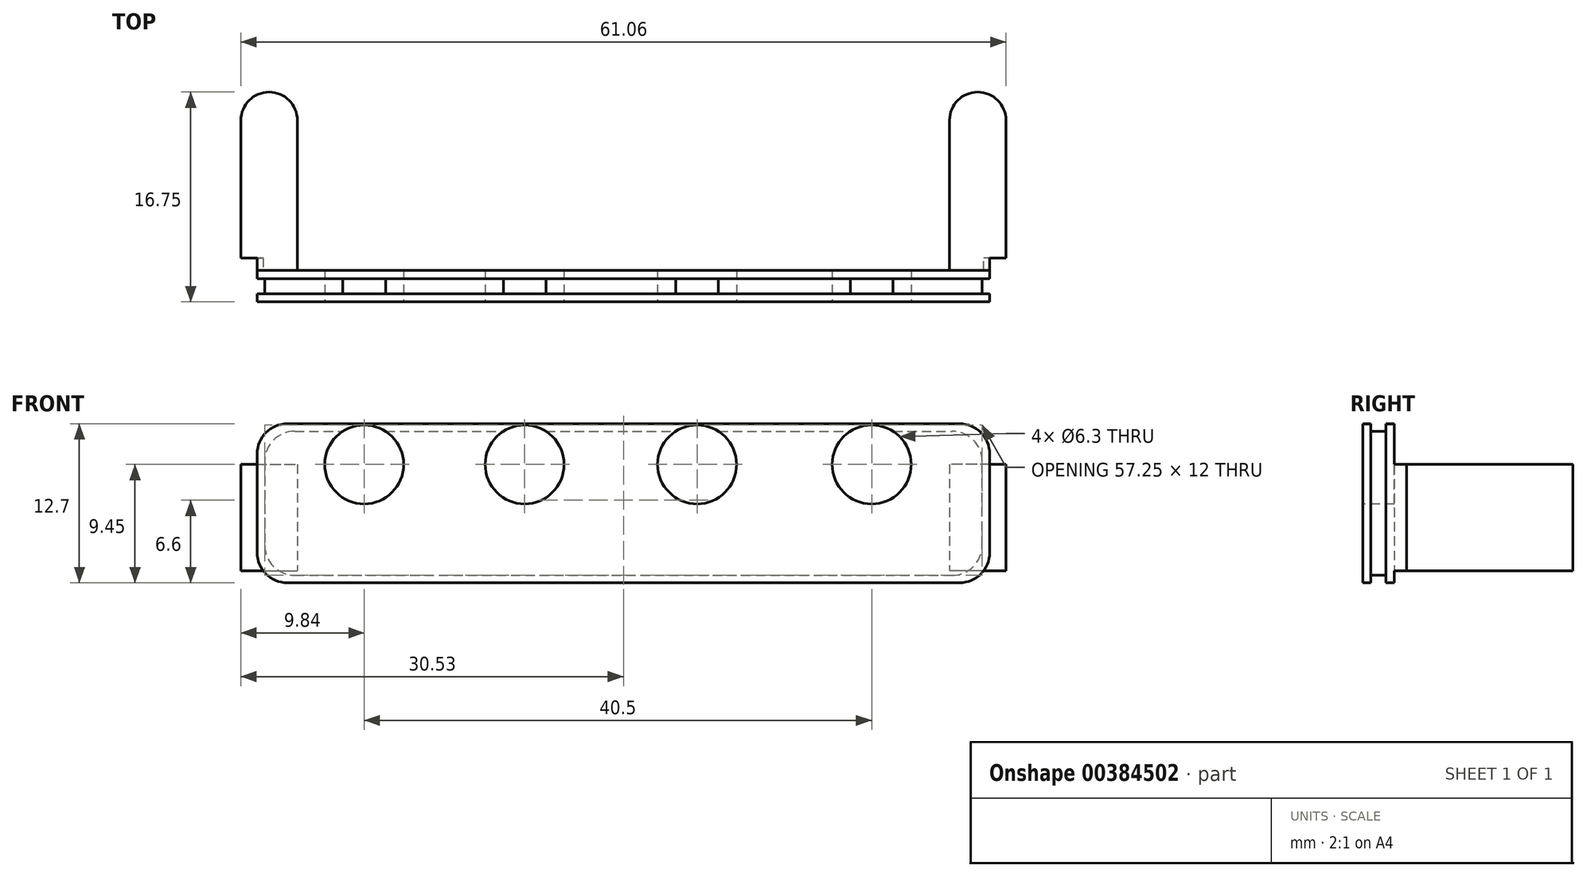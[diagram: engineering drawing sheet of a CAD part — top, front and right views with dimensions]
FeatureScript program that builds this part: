
annotation { "Feature Type Name" : "Feature", "Feature Type Description" : "" }
export const myFeature = defineFeature(function(context is Context, id is Id, definition is map)
    precondition{}
    {
        {
            var Q0;
            Q0=qCreatedBy(makeId("Front.planeOp"),FACE);
            var sketch = newSketch(context, id + "F0", { "sketchPlane" : qUnion([Q0])});
            skLineSegment(sketch, "E0.bottom", {"start": v(29.22, -6.35) * mm, "end": v(-29.23, -6.35) * mm});
            skLineSegment(sketch, "E0.top", {"start": v(29.23, 6.35) * mm, "end": v(-29.23, 6.35) * mm});
            skLineSegment(sketch, "E0.left", {"start": v(29.23, -6.35) * mm, "end": v(29.23, 6.35) * mm});
            skLineSegment(sketch, "E0.right", {"start": v(-29.23, -6.35) * mm, "end": v(-29.23, 6.35) * mm});
            skPoint(sketch, "E0.middle", {"position": v(0, 0) * mm});
            skSolve(sketch);
        }
        {
            var Q0;
            Q0 = qSketchRegion(id + "F0", true);
            extrude(context, id + "F1", {"entities" : qUnion([Q0]), "oppositeDirection" : true, "depth" : 2.5 * mm});
        }
        {
            var Q0;
            Q0=makeQuery(id+"F1.opExtrude","SWEPT_FACE",FACE,{"disambiguationData":[OSD([sQuery(id+"F0.wireOp",EDGE,"E0.top")])]});
            var sketch = newSketch(context, id + "F2", { "sketchPlane" : qUnion([Q0])});
            skLineSegment(sketch, "E1.bottom", {"start": v(-29.23, 1.85) * mm, "end": v(29.23, 1.85) * mm});
            skLineSegment(sketch, "E1.top", {"start": v(-29.23, 0.64) * mm, "end": v(29.23, 0.64) * mm});
            skLineSegment(sketch, "E1.left", {"start": v(-29.23, 1.85) * mm, "end": v(-29.23, 0.64) * mm});
            skLineSegment(sketch, "E1.right", {"start": v(29.23, 1.85) * mm, "end": v(29.23, 0.64) * mm});
            skSolve(sketch);
        }
        {
            var Q0;
            Q0=makeQuery(id+"F1.opExtrude","SWEPT_FACE",FACE,{"disambiguationData":[OSD([sQuery(id+"F0.wireOp",EDGE,"E0.right")])]});
            var sketch = newSketch(context, id + "F3", { "sketchPlane" : qUnion([Q0])});
            skLineSegment(sketch, "E2.bottom", {"start": v(-1.85, 6.35) * mm, "end": v(-0.64, 6.35) * mm});
            skLineSegment(sketch, "E2.top", {"start": v(-1.85, -6.35) * mm, "end": v(-0.64, -6.35) * mm});
            skLineSegment(sketch, "E2.left", {"start": v(-1.85, 6.35) * mm, "end": v(-1.85, -6.35) * mm});
            skLineSegment(sketch, "E2.right", {"start": v(-0.64, 6.35) * mm, "end": v(-0.64, -6.35) * mm});
            skSolve(sketch);
        }
        {
            var Q0;
            Q0=makeQuery(id+"F1.opExtrude","SWEPT_FACE",FACE,{"disambiguationData":[OSD([sQuery(id+"F0.wireOp",EDGE,"E0.bottom")])]});
            var sketch = newSketch(context, id + "F4", { "sketchPlane" : qUnion([Q0])});
            skLineSegment(sketch, "E3.bottom", {"start": v(-29.23, -1.85) * mm, "end": v(29.23, -1.85) * mm});
            skLineSegment(sketch, "E3.top", {"start": v(-29.23, -0.64) * mm, "end": v(29.23, -0.64) * mm});
            skLineSegment(sketch, "E3.left", {"start": v(-29.23, -1.85) * mm, "end": v(-29.23, -0.64) * mm});
            skLineSegment(sketch, "E3.right", {"start": v(29.22, -1.85) * mm, "end": v(29.22, -0.64) * mm});
            skSolve(sketch);
        }
        {
            var Q0;
            Q0=makeQuery(id+"F1.opExtrude","SWEPT_FACE",FACE,{"disambiguationData":[OSD([sQuery(id+"F0.wireOp",EDGE,"E0.left")])]});
            var sketch = newSketch(context, id + "F5", { "sketchPlane" : qUnion([Q0])});
            skLineSegment(sketch, "E4.bottom", {"start": v(1.85, -6.35) * mm, "end": v(0.64, -6.35) * mm});
            skLineSegment(sketch, "E4.top", {"start": v(1.85, 6.35) * mm, "end": v(0.64, 6.35) * mm});
            skLineSegment(sketch, "E4.left", {"start": v(1.85, -6.35) * mm, "end": v(1.85, 6.35) * mm});
            skLineSegment(sketch, "E4.right", {"start": v(0.64, -6.35) * mm, "end": v(0.64, 6.35) * mm});
            skSolve(sketch);
        }
        {
            var Q0;
            Q0=makeQuery(id+"F2.imprint","IMPRINT",FACE,{"disambiguationData":[TD([[makeQuery(id+"F2.imprint","IMPRINT",EDGE,{"derivedFrom":sQuery(id+"F2.wireOp",EDGE,"E1.bottom")}),-1.0]])]});
            extrude(context, id + "F6", {"entities" : qUnion([Q0]), "operationType" : NewBodyOperationType.REMOVE, "oppositeDirection" : true, "depth" : 0.6 * mm});
        }
        {
            var Q0;
            Q0=makeQuery(id+"F4.imprint","IMPRINT",FACE,{"disambiguationData":[TD([[makeQuery(id+"F4.imprint","IMPRINT",EDGE,{"derivedFrom":sQuery(id+"F4.wireOp",EDGE,"E3.bottom")}),1.0]])]});
            extrude(context, id + "F7", {"entities" : qUnion([Q0]), "operationType" : NewBodyOperationType.REMOVE, "oppositeDirection" : true, "depth" : 0.6 * mm});
        }
        {
            var Q0;
            Q0=makeQuery(id+"F5.imprint","IMPRINT",FACE,{"disambiguationData":[TD([[makeQuery(id+"F5.imprint","IMPRINT",EDGE,{"derivedFrom":sQuery(id+"F5.wireOp",EDGE,"E4.bottom")}),-1.0]])]});
            extrude(context, id + "F8", {"entities" : qUnion([Q0]), "operationType" : NewBodyOperationType.REMOVE, "oppositeDirection" : true, "depth" : 0.6 * mm});
        }
        {
            var Q0;
            Q0=makeQuery(id+"F3.imprint","IMPRINT",FACE,{"disambiguationData":[TD([[makeQuery(id+"F3.imprint","IMPRINT",EDGE,{"derivedFrom":sQuery(id+"F3.wireOp",EDGE,"E2.bottom")}),-1.0]])]});
            extrude(context, id + "F9", {"entities" : qUnion([Q0]), "operationType" : NewBodyOperationType.REMOVE, "oppositeDirection" : true, "depth" : 0.6 * mm});
        }
        {
            var Q0;
            Q0=makeQuery(id+"F1.opExtrude","CAP_FACE",FACE,{"disambiguationData":[OSD([sQuery(id+"F0.wireOp",EDGE,"E0.bottom"),sQuery(id+"F0.wireOp",EDGE,"E0.top"),sQuery(id+"F0.wireOp",EDGE,"E0.left"),sQuery(id+"F0.wireOp",EDGE,"E0.right")])],"isStart":false});
            var sketch = newSketch(context, id + "F10", { "sketchPlane" : qUnion([Q0])});
            skLineSegment(sketch, "E5.bottom", {"start": v(-29.23, 3.1) * mm, "end": v(-26.02, 3.1) * mm});
            skLineSegment(sketch, "E5.top", {"start": v(-29.23, -5.4) * mm, "end": v(-26.02, -5.4) * mm});
            skLineSegment(sketch, "E5.left", {"start": v(-29.23, 3.1) * mm, "end": v(-29.23, -5.4) * mm});
            skLineSegment(sketch, "E5.right", {"start": v(-26.02, 3.1) * mm, "end": v(-26.02, -5.4) * mm});
            skLineSegment(sketch, "E6.bottom", {"start": v(29.23, 3.1) * mm, "end": v(26.02, 3.1) * mm});
            skLineSegment(sketch, "E6.top", {"start": v(29.23, -5.4) * mm, "end": v(26.02, -5.4) * mm});
            skLineSegment(sketch, "E6.left", {"start": v(29.23, 3.1) * mm, "end": v(29.23, -5.4) * mm});
            skLineSegment(sketch, "E6.right", {"start": v(26.02, 3.1) * mm, "end": v(26.02, -5.4) * mm});
            skSolve(sketch);
        }
        {
            var Q0;
            Q0 = qSketchRegion(id + "F10", true);
            extrude(context, id + "F11", {"entities" : qUnion([Q0]), "operationType" : NewBodyOperationType.ADD, "depth" : 1 * mm});
        }
        {
            var Q0;
            {var subQ0=sQuery(id+"F0.wireOp",EDGE,"E0.bottom");var subQ1=sQuery(id+"F0.wireOp",EDGE,"E0.right");Q0=makeQuery(id+"F7.boolean.opBoolean","SPLIT",EDGE,{"disambiguationData":[TD([makeQuery(id+"F7.opExtrude","SWEPT_FACE",FACE,{"disambiguationData":[OSD([sQuery(id+"F4.wireOp",EDGE,"E3.bottom")])]})])],"derivedFrom":makeQuery(id+"F1.opExtrude","SWEPT_EDGE",EDGE,{"disambiguationData":[OSD([subQ0,subQ1])]})});}
            var Q1;
            Q1=makeQuery(id+"F9.boolean.opBoolean","INTERSECT",EDGE,{"derivedFrom":[makeQuery(id+"F7.boolean.opBoolean","COPY",FACE,{"derivedFrom":makeQuery(id+"F7.opExtrude","CAP_FACE",FACE,{"disambiguationData":[OSD([sQuery(id+"F4.wireOp",EDGE,"E3.bottom"),sQuery(id+"F4.wireOp",EDGE,"E3.top"),sQuery(id+"F4.wireOp",EDGE,"E3.left"),sQuery(id+"F4.wireOp",EDGE,"E3.right")])],"isStart":false})}),makeQuery(id+"F9.opExtrude","CAP_FACE",FACE,{"disambiguationData":[OSD([sQuery(id+"F3.wireOp",EDGE,"E2.bottom"),sQuery(id+"F3.wireOp",EDGE,"E2.top"),sQuery(id+"F3.wireOp",EDGE,"E2.left"),sQuery(id+"F3.wireOp",EDGE,"E2.right")])],"isStart":false})]});
            var Q2;
            {var subQ0=sQuery(id+"F0.wireOp",EDGE,"E0.bottom");var subQ1=sQuery(id+"F0.wireOp",EDGE,"E0.right");Q2=makeQuery(id+"F7.boolean.opBoolean","SPLIT",EDGE,{"disambiguationData":[TD([makeQuery(id+"F7.opExtrude","SWEPT_FACE",FACE,{"disambiguationData":[OSD([sQuery(id+"F4.wireOp",EDGE,"E3.top")])]})])],"derivedFrom":makeQuery(id+"F1.opExtrude","SWEPT_EDGE",EDGE,{"disambiguationData":[OSD([subQ0,subQ1])]})});}
            var Q3;
            {var subQ0=sQuery(id+"F0.wireOp",EDGE,"E0.right");var subQ1=sQuery(id+"F0.wireOp",EDGE,"E0.top");Q3=makeQuery(id+"F6.boolean.opBoolean","SPLIT",EDGE,{"disambiguationData":[TD([makeQuery(id+"F6.opExtrude","SWEPT_FACE",FACE,{"disambiguationData":[OSD([sQuery(id+"F2.wireOp",EDGE,"E1.top")])]})])],"derivedFrom":makeQuery(id+"F1.opExtrude","SWEPT_EDGE",EDGE,{"disambiguationData":[OSD([subQ1,subQ0])]})});}
            var Q4;
            Q4=makeQuery(id+"F9.boolean.opBoolean","INTERSECT",EDGE,{"derivedFrom":[makeQuery(id+"F6.boolean.opBoolean","COPY",FACE,{"derivedFrom":makeQuery(id+"F6.opExtrude","CAP_FACE",FACE,{"disambiguationData":[OSD([sQuery(id+"F2.wireOp",EDGE,"E1.bottom"),sQuery(id+"F2.wireOp",EDGE,"E1.top"),sQuery(id+"F2.wireOp",EDGE,"E1.left"),sQuery(id+"F2.wireOp",EDGE,"E1.right")])],"isStart":false})}),makeQuery(id+"F9.opExtrude","CAP_FACE",FACE,{"disambiguationData":[OSD([sQuery(id+"F3.wireOp",EDGE,"E2.bottom"),sQuery(id+"F3.wireOp",EDGE,"E2.top"),sQuery(id+"F3.wireOp",EDGE,"E2.left"),sQuery(id+"F3.wireOp",EDGE,"E2.right")])],"isStart":false})]});
            var Q5;
            {var subQ0=sQuery(id+"F0.wireOp",EDGE,"E0.right");var subQ1=sQuery(id+"F0.wireOp",EDGE,"E0.top");Q5=makeQuery(id+"F6.boolean.opBoolean","SPLIT",EDGE,{"disambiguationData":[TD([makeQuery(id+"F6.opExtrude","SWEPT_FACE",FACE,{"disambiguationData":[OSD([sQuery(id+"F2.wireOp",EDGE,"E1.bottom")])]})])],"derivedFrom":makeQuery(id+"F1.opExtrude","SWEPT_EDGE",EDGE,{"disambiguationData":[OSD([subQ1,subQ0])]})});}
            var Q6;
            {var subQ0=sQuery(id+"F0.wireOp",EDGE,"E0.left");var subQ1=sQuery(id+"F0.wireOp",EDGE,"E0.top");Q6=makeQuery(id+"F6.boolean.opBoolean","SPLIT",EDGE,{"disambiguationData":[TD([makeQuery(id+"F6.opExtrude","SWEPT_FACE",FACE,{"disambiguationData":[OSD([sQuery(id+"F2.wireOp",EDGE,"E1.top")])]})])],"derivedFrom":makeQuery(id+"F1.opExtrude","SWEPT_EDGE",EDGE,{"disambiguationData":[OSD([subQ1,subQ0])]})});}
            var Q7;
            Q7=makeQuery(id+"F8.boolean.opBoolean","INTERSECT",EDGE,{"derivedFrom":[makeQuery(id+"F6.boolean.opBoolean","COPY",FACE,{"derivedFrom":makeQuery(id+"F6.opExtrude","CAP_FACE",FACE,{"disambiguationData":[OSD([sQuery(id+"F2.wireOp",EDGE,"E1.bottom"),sQuery(id+"F2.wireOp",EDGE,"E1.top"),sQuery(id+"F2.wireOp",EDGE,"E1.left"),sQuery(id+"F2.wireOp",EDGE,"E1.right")])],"isStart":false})}),makeQuery(id+"F8.opExtrude","CAP_FACE",FACE,{"disambiguationData":[OSD([sQuery(id+"F5.wireOp",EDGE,"E4.bottom"),sQuery(id+"F5.wireOp",EDGE,"E4.top"),sQuery(id+"F5.wireOp",EDGE,"E4.left"),sQuery(id+"F5.wireOp",EDGE,"E4.right")])],"isStart":false})]});
            var Q8;
            {var subQ0=sQuery(id+"F0.wireOp",EDGE,"E0.left");var subQ1=sQuery(id+"F0.wireOp",EDGE,"E0.top");Q8=makeQuery(id+"F6.boolean.opBoolean","SPLIT",EDGE,{"disambiguationData":[TD([makeQuery(id+"F6.opExtrude","SWEPT_FACE",FACE,{"disambiguationData":[OSD([sQuery(id+"F2.wireOp",EDGE,"E1.bottom")])]})])],"derivedFrom":makeQuery(id+"F1.opExtrude","SWEPT_EDGE",EDGE,{"disambiguationData":[OSD([subQ1,subQ0])]})});}
            var Q9;
            {var subQ0=sQuery(id+"F0.wireOp",EDGE,"E0.bottom");var subQ1=sQuery(id+"F0.wireOp",EDGE,"E0.left");Q9=makeQuery(id+"F7.boolean.opBoolean","SPLIT",EDGE,{"disambiguationData":[TD([makeQuery(id+"F7.opExtrude","SWEPT_FACE",FACE,{"disambiguationData":[OSD([sQuery(id+"F4.wireOp",EDGE,"E3.top")])]})])],"derivedFrom":makeQuery(id+"F1.opExtrude","SWEPT_EDGE",EDGE,{"disambiguationData":[OSD([subQ0,subQ1])]})});}
            var Q10;
            Q10=makeQuery(id+"F8.boolean.opBoolean","INTERSECT",EDGE,{"derivedFrom":[makeQuery(id+"F7.boolean.opBoolean","COPY",FACE,{"derivedFrom":makeQuery(id+"F7.opExtrude","CAP_FACE",FACE,{"disambiguationData":[OSD([sQuery(id+"F4.wireOp",EDGE,"E3.bottom"),sQuery(id+"F4.wireOp",EDGE,"E3.top"),sQuery(id+"F4.wireOp",EDGE,"E3.left"),sQuery(id+"F4.wireOp",EDGE,"E3.right")])],"isStart":false})}),makeQuery(id+"F8.opExtrude","CAP_FACE",FACE,{"disambiguationData":[OSD([sQuery(id+"F5.wireOp",EDGE,"E4.bottom"),sQuery(id+"F5.wireOp",EDGE,"E4.top"),sQuery(id+"F5.wireOp",EDGE,"E4.left"),sQuery(id+"F5.wireOp",EDGE,"E4.right")])],"isStart":false})]});
            var Q11;
            {var subQ0=sQuery(id+"F0.wireOp",EDGE,"E0.bottom");var subQ1=sQuery(id+"F0.wireOp",EDGE,"E0.left");Q11=makeQuery(id+"F7.boolean.opBoolean","SPLIT",EDGE,{"disambiguationData":[TD([makeQuery(id+"F7.opExtrude","SWEPT_FACE",FACE,{"disambiguationData":[OSD([sQuery(id+"F4.wireOp",EDGE,"E3.bottom")])]})])],"derivedFrom":makeQuery(id+"F1.opExtrude","SWEPT_EDGE",EDGE,{"disambiguationData":[OSD([subQ0,subQ1])]})});}
            fillet(context, id + "F12", {"entities" : qUnion([Q0, Q1, Q2, Q3, Q4, Q5, Q6, Q7, Q8, Q9, Q10, Q11]), "radius" : 2.4 * mm, "tangentPropagation" : true, "allowEdgeOverflow" : false});
        }
        {
            var Q0;
            Q0=makeQuery(id+"F11.opExtrude","CAP_FACE",FACE,{"disambiguationData":[OSD([sQuery(id+"F10.wireOp",EDGE,"E5.bottom"),sQuery(id+"F10.wireOp",EDGE,"E5.top"),sQuery(id+"F10.wireOp",EDGE,"E5.left"),sQuery(id+"F10.wireOp",EDGE,"E5.right")])],"isStart":false});
            var sketch = newSketch(context, id + "F13", { "sketchPlane" : qUnion([Q0])});
            skLineSegment(sketch, "E7.bottom", {"start": v(-26.02, 3.1) * mm, "end": v(-30.52, 3.1) * mm});
            skLineSegment(sketch, "E7.top", {"start": v(-26.02, -5.4) * mm, "end": v(-30.52, -5.4) * mm});
            skLineSegment(sketch, "E7.left", {"start": v(-26.02, 3.1) * mm, "end": v(-26.02, -5.4) * mm});
            skLineSegment(sketch, "E7.right", {"start": v(-30.52, 3.1) * mm, "end": v(-30.52, -5.4) * mm});
            skSolve(sketch);
        }
        {
            var Q0;
            Q0=makeQuery(id+"F11.opExtrude","CAP_FACE",FACE,{"disambiguationData":[OSD([sQuery(id+"F10.wireOp",EDGE,"E6.bottom"),sQuery(id+"F10.wireOp",EDGE,"E6.top"),sQuery(id+"F10.wireOp",EDGE,"E6.left"),sQuery(id+"F10.wireOp",EDGE,"E6.right")])],"isStart":false});
            var sketch = newSketch(context, id + "F14", { "sketchPlane" : qUnion([Q0])});
            skPoint(sketch, "E8.oppositeSnap0", {"position": v(27.38, -5.4) * mm});
            skLineSegment(sketch, "E8.bottom", {"start": v(26.02, 3.1) * mm, "end": v(30.52, 3.1) * mm});
            skLineSegment(sketch, "E8.top", {"start": v(26.02, -5.4) * mm, "end": v(30.52, -5.4) * mm});
            skLineSegment(sketch, "E8.left", {"start": v(26.02, 3.1) * mm, "end": v(26.02, -5.4) * mm});
            skLineSegment(sketch, "E8.right", {"start": v(30.52, 3.1) * mm, "end": v(30.52, -5.4) * mm});
            skSolve(sketch);
        }
        {
            var Q0;
            Q0 = qSketchRegion(id + "F14", true);
            var Q1;
            Q1 = qSketchRegion(id + "F13", true);
            extrude(context, id + "F15", {"entities" : qUnion([Q0, Q1]), "operationType" : NewBodyOperationType.ADD, "depth" : 13.25 * mm});
        }
        {
            var Q0;
            Q0=makeQuery(id+"F15.opExtrude","CAP_EDGE",EDGE,{"disambiguationData":[OSD([sQuery(id+"F13.wireOp",EDGE,"E7.left")])],"isStart":false});
            var Q1;
            Q1=makeQuery(id+"F15.opExtrude","CAP_EDGE",EDGE,{"disambiguationData":[OSD([sQuery(id+"F13.wireOp",EDGE,"E7.right")])],"isStart":false});
            var Q2;
            Q2=makeQuery(id+"F15.opExtrude","CAP_EDGE",EDGE,{"disambiguationData":[OSD([sQuery(id+"F14.wireOp",EDGE,"E8.left")])],"isStart":false});
            var Q3;
            Q3=makeQuery(id+"F15.opExtrude","CAP_EDGE",EDGE,{"disambiguationData":[OSD([sQuery(id+"F14.wireOp",EDGE,"E8.right")])],"isStart":false});
            fillet(context, id + "F16", {"entities" : qUnion([Q0, Q1, Q2, Q3]), "radius" : 2.25 * mm, "tangentPropagation" : true, "allowEdgeOverflow" : false});
        }
        {
            var Q0;
            Q0=makeQuery(id+"F1.opExtrude","CAP_FACE",FACE,{"disambiguationData":[OSD([sQuery(id+"F0.wireOp",EDGE,"E0.bottom"),sQuery(id+"F0.wireOp",EDGE,"E0.top"),sQuery(id+"F0.wireOp",EDGE,"E0.left"),sQuery(id+"F0.wireOp",EDGE,"E0.right")])],"isStart":true});
            var sketch = newSketch(context, id + "F17", { "sketchPlane" : qUnion([Q0])});
            skCircle(sketch, "E9", {"center": v(19.8, 3.1) * mm, "radius": 3.15 * mm});
            skCircle(sketch, "E10", {"center": v(5.88, 3.1) * mm, "radius": 3.15 * mm});
            skCircle(sketch, "E11", {"center": v(-7.89, 3.1) * mm, "radius": 3.15 * mm});
            skCircle(sketch, "E12", {"center": v(-20.7, 3.1) * mm, "radius": 3.15 * mm});
            skSolve(sketch);
        }
        {
            var Q0;
            Q0 = qSketchRegion(id + "F17", true);
            extrude(context, id + "F18", {"entities" : qUnion([Q0]), "operationType" : NewBodyOperationType.REMOVE, "endBound" : BoundingType.THROUGH_ALL, "oppositeDirection" : true, "depth" : 25 * mm});
        }
    });
